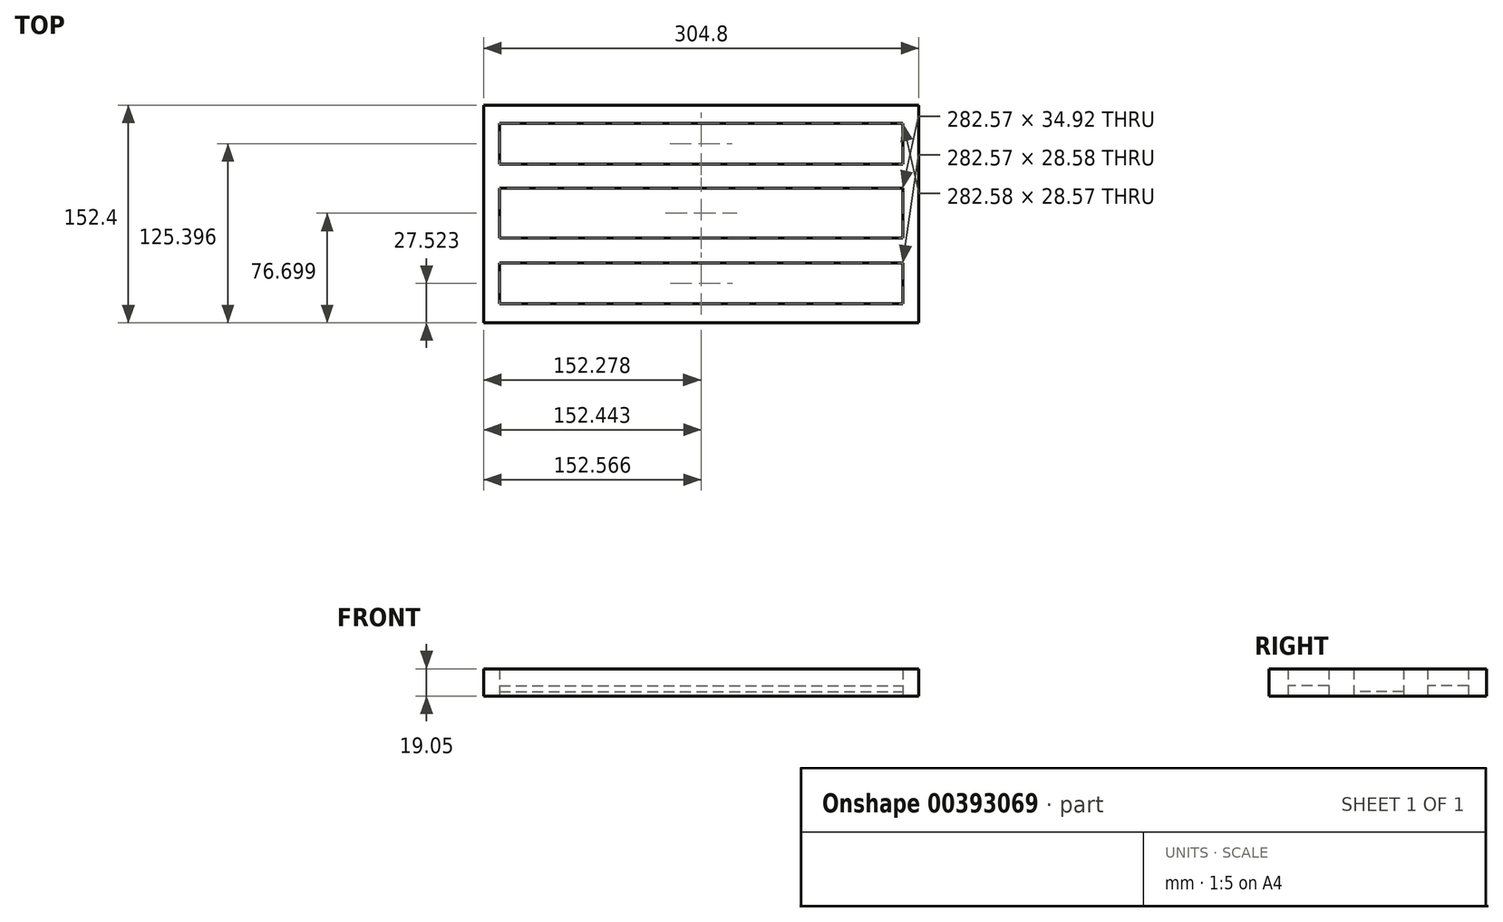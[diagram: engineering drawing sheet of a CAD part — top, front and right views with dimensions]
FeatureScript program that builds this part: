
annotation { "Feature Type Name" : "Feature", "Feature Type Description" : "" }
export const myFeature = defineFeature(function(context is Context, id is Id, definition is map)
    precondition{}
    {
        {
            var Q0;
            Q0=qCreatedBy(makeId("Top.planeOp"),FACE);
            var sketch = newSketch(context, id + "F0", { "sketchPlane" : qUnion([Q0])});
            skLineSegment(sketch, "E0.bottom", {"start": v(-138.77, 34.95) * mm, "end": v(166.03, 34.95) * mm});
            skLineSegment(sketch, "E0.top", {"start": v(-138.77, -117.45) * mm, "end": v(166.03, -117.45) * mm});
            skLineSegment(sketch, "E0.left", {"start": v(-138.77, 34.95) * mm, "end": v(-138.77, -117.45) * mm});
            skLineSegment(sketch, "E0.right", {"start": v(166.03, 34.95) * mm, "end": v(166.03, -117.45) * mm});
            skLineSegment(sketch, "E1.bottom", {"start": v(-127.78, 22.23) * mm, "end": v(154.8, 22.23) * mm});
            skLineSegment(sketch, "E1.top", {"start": v(-127.78, -6.34) * mm, "end": v(154.8, -6.34) * mm});
            skLineSegment(sketch, "E1.left", {"start": v(-127.78, 22.23) * mm, "end": v(-127.78, -6.34) * mm});
            skLineSegment(sketch, "E1.right", {"start": v(154.8, 22.23) * mm, "end": v(154.8, -6.34) * mm});
            skLineSegment(sketch, "E2.bottom", {"start": v(-127.5, -75.64) * mm, "end": v(155.08, -75.64) * mm});
            skLineSegment(sketch, "E2.top", {"start": v(-127.5, -104.21) * mm, "end": v(155.08, -104.21) * mm});
            skLineSegment(sketch, "E2.left", {"start": v(-127.5, -75.64) * mm, "end": v(-127.5, -104.21) * mm});
            skLineSegment(sketch, "E2.right", {"start": v(155.08, -75.64) * mm, "end": v(155.08, -104.21) * mm});
            skLineSegment(sketch, "E3.bottom", {"start": v(-127.61, -23.29) * mm, "end": v(154.96, -23.29) * mm});
            skLineSegment(sketch, "E3.top", {"start": v(-127.61, -58.21) * mm, "end": v(154.96, -58.21) * mm});
            skLineSegment(sketch, "E3.left", {"start": v(-127.61, -23.29) * mm, "end": v(-127.61, -58.21) * mm});
            skLineSegment(sketch, "E3.right", {"start": v(154.96, -23.29) * mm, "end": v(154.96, -58.21) * mm});
            skSolve(sketch);
        }
        {
            var Q0;
            Q0=makeQuery(id+"F0.imprint","IMPRINT",FACE,{"disambiguationData":[TD([[makeQuery(id+"F0.imprint","IMPRINT",EDGE,{"derivedFrom":sQuery(id+"F0.wireOp",EDGE,"E2.bottom")}),-1.0]])]});
            var Q1;
            Q1=makeQuery(id+"F0.imprint","IMPRINT",FACE,{"disambiguationData":[TD([[makeQuery(id+"F0.imprint","IMPRINT",EDGE,{"derivedFrom":sQuery(id+"F0.wireOp",EDGE,"E1.bottom")}),-1.0]])]});
            extrude(context, id + "F1", {"entities" : qUnion([Q0, Q1]), "depth" : 7.32 * mm});
        }
        {
            var Q0;
            Q0=makeQuery(id+"F0.imprint","IMPRINT",FACE,{"disambiguationData":[TD([[makeQuery(id+"F0.imprint","IMPRINT",EDGE,{"derivedFrom":sQuery(id+"F0.wireOp",EDGE,"E3.bottom")}),-1.0]])]});
            extrude(context, id + "F2", {"entities" : qUnion([Q0]), "depth" : 3.17 * mm});
        }
        {
            var Q0;
            Q0=makeQuery(id+"F0.imprint","IMPRINT",FACE,{"disambiguationData":[TD([[makeQuery(id+"F0.imprint","IMPRINT",EDGE,{"derivedFrom":sQuery(id+"F0.wireOp",EDGE,"E0.bottom")}),-1.0]])]});
            extrude(context, id + "F3", {"entities" : qUnion([Q0]), "depth" : 19.05 * mm});
        }
    });
